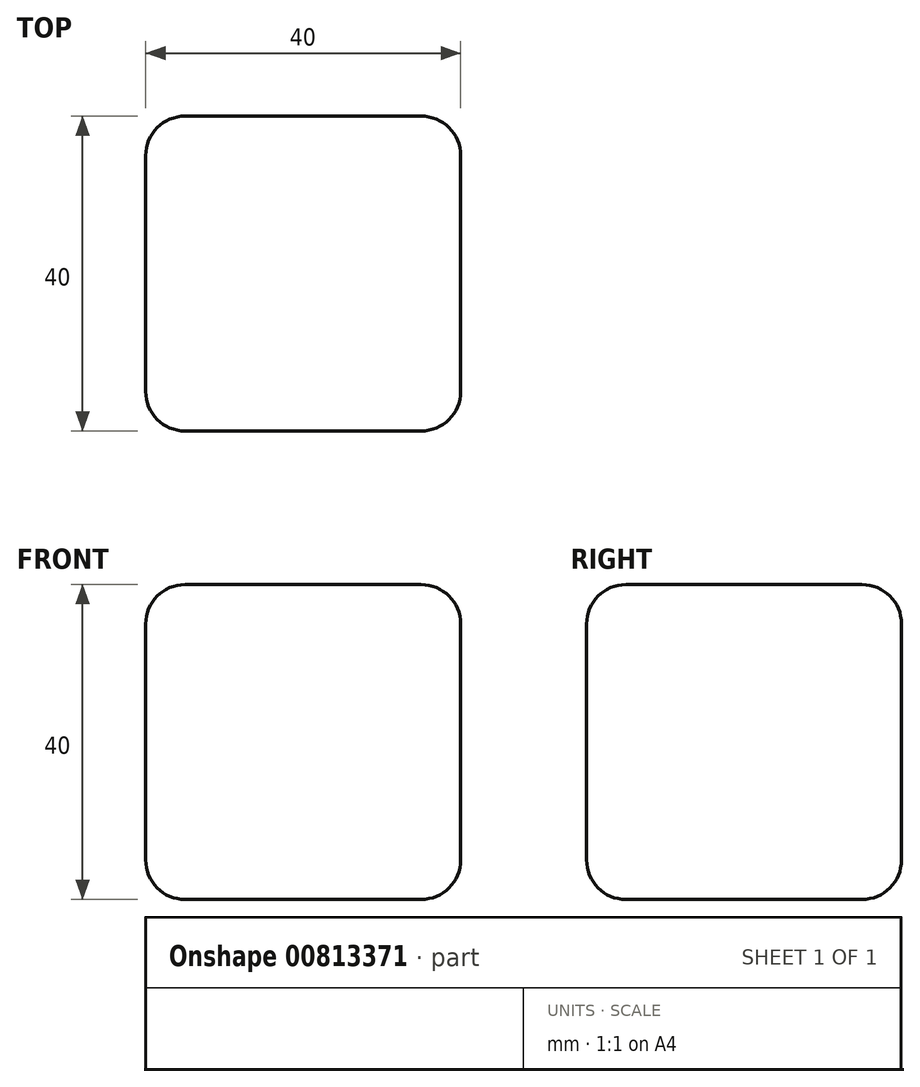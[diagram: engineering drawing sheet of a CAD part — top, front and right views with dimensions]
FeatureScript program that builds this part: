
annotation { "Feature Type Name" : "Feature", "Feature Type Description" : "" }
export const myFeature = defineFeature(function(context is Context, id is Id, definition is map)
    precondition{}
    {
        {
            var Q0;
            Q0=qCreatedBy(makeId("Front.planeOp"),FACE);
            var sketch = newSketch(context, id + "F0", { "sketchPlane" : qUnion([Q0])});
            skLineSegment(sketch, "E0.bottom", {"start": v(0.11, 31.29) * mm, "end": v(40.11, 31.29) * mm});
            skLineSegment(sketch, "E0.top", {"start": v(0.11, -8.71) * mm, "end": v(40.11, -8.71) * mm});
            skLineSegment(sketch, "E0.left", {"start": v(0.11, 31.29) * mm, "end": v(0.11, -8.71) * mm});
            skLineSegment(sketch, "E0.right", {"start": v(40.11, 31.29) * mm, "end": v(40.11, -8.71) * mm});
            skSolve(sketch);
        }
        {
            var Q0;
            Q0 = qSketchRegion(id + "F0", true);
            extrude(context, id + "F1", {"entities" : qUnion([Q0]), "depth" : 40 * mm, "offsetDistance" : 25 * mm});
        }
        {
            var Q0;
            Q0=makeQuery(id+"F1.opExtrude","CAP_EDGE",EDGE,{"disambiguationData":[OSD([sQuery(id+"F0.wireOp",EDGE,"E0.left")])],"isStart":true});
            var Q1;
            Q1=makeQuery(id+"F1.opExtrude","CAP_EDGE",EDGE,{"disambiguationData":[OSD([sQuery(id+"F0.wireOp",EDGE,"E0.bottom")])],"isStart":true});
            var Q2;
            Q2=makeQuery(id+"F1.opExtrude","CAP_EDGE",EDGE,{"disambiguationData":[OSD([sQuery(id+"F0.wireOp",EDGE,"E0.top")])],"isStart":true});
            var Q3;
            Q3=makeQuery(id+"F1.opExtrude","CAP_EDGE",EDGE,{"disambiguationData":[OSD([sQuery(id+"F0.wireOp",EDGE,"E0.right")])],"isStart":true});
            var Q4;
            Q4=makeQuery(id+"F1.opExtrude","SWEPT_EDGE",EDGE,{"disambiguationData":[OSD([sQuery(id+"F0.wireOp",EDGE,"E0.top"),sQuery(id+"F0.wireOp",EDGE,"E0.right")])]});
            var Q5;
            Q5=makeQuery(id+"F1.opExtrude","SWEPT_EDGE",EDGE,{"disambiguationData":[OSD([sQuery(id+"F0.wireOp",EDGE,"E0.top"),sQuery(id+"F0.wireOp",EDGE,"E0.left")])]});
            var Q6;
            Q6=makeQuery(id+"F1.opExtrude","SWEPT_EDGE",EDGE,{"disambiguationData":[OSD([sQuery(id+"F0.wireOp",EDGE,"E0.bottom"),sQuery(id+"F0.wireOp",EDGE,"E0.left")])]});
            var Q7;
            Q7=makeQuery(id+"F1.opExtrude","SWEPT_EDGE",EDGE,{"disambiguationData":[OSD([sQuery(id+"F0.wireOp",EDGE,"E0.bottom"),sQuery(id+"F0.wireOp",EDGE,"E0.right")])]});
            var Q8;
            Q8=makeQuery(id+"F1.opExtrude","CAP_EDGE",EDGE,{"disambiguationData":[OSD([sQuery(id+"F0.wireOp",EDGE,"E0.bottom")])],"isStart":false});
            var Q9;
            Q9=makeQuery(id+"F1.opExtrude","CAP_EDGE",EDGE,{"disambiguationData":[OSD([sQuery(id+"F0.wireOp",EDGE,"E0.left")])],"isStart":false});
            var Q10;
            Q10=makeQuery(id+"F1.opExtrude","CAP_EDGE",EDGE,{"disambiguationData":[OSD([sQuery(id+"F0.wireOp",EDGE,"E0.top")])],"isStart":false});
            var Q11;
            Q11=makeQuery(id+"F1.opExtrude","CAP_EDGE",EDGE,{"disambiguationData":[OSD([sQuery(id+"F0.wireOp",EDGE,"E0.right")])],"isStart":false});
            fillet(context, id + "F2", {"entities" : qUnion([Q0, Q1, Q2, Q3, Q4, Q5, Q6, Q7, Q8, Q9, Q10, Q11]), "radius" : 5 * mm, "tangentPropagation" : true, "allowEdgeOverflow" : false});
        }
    });
